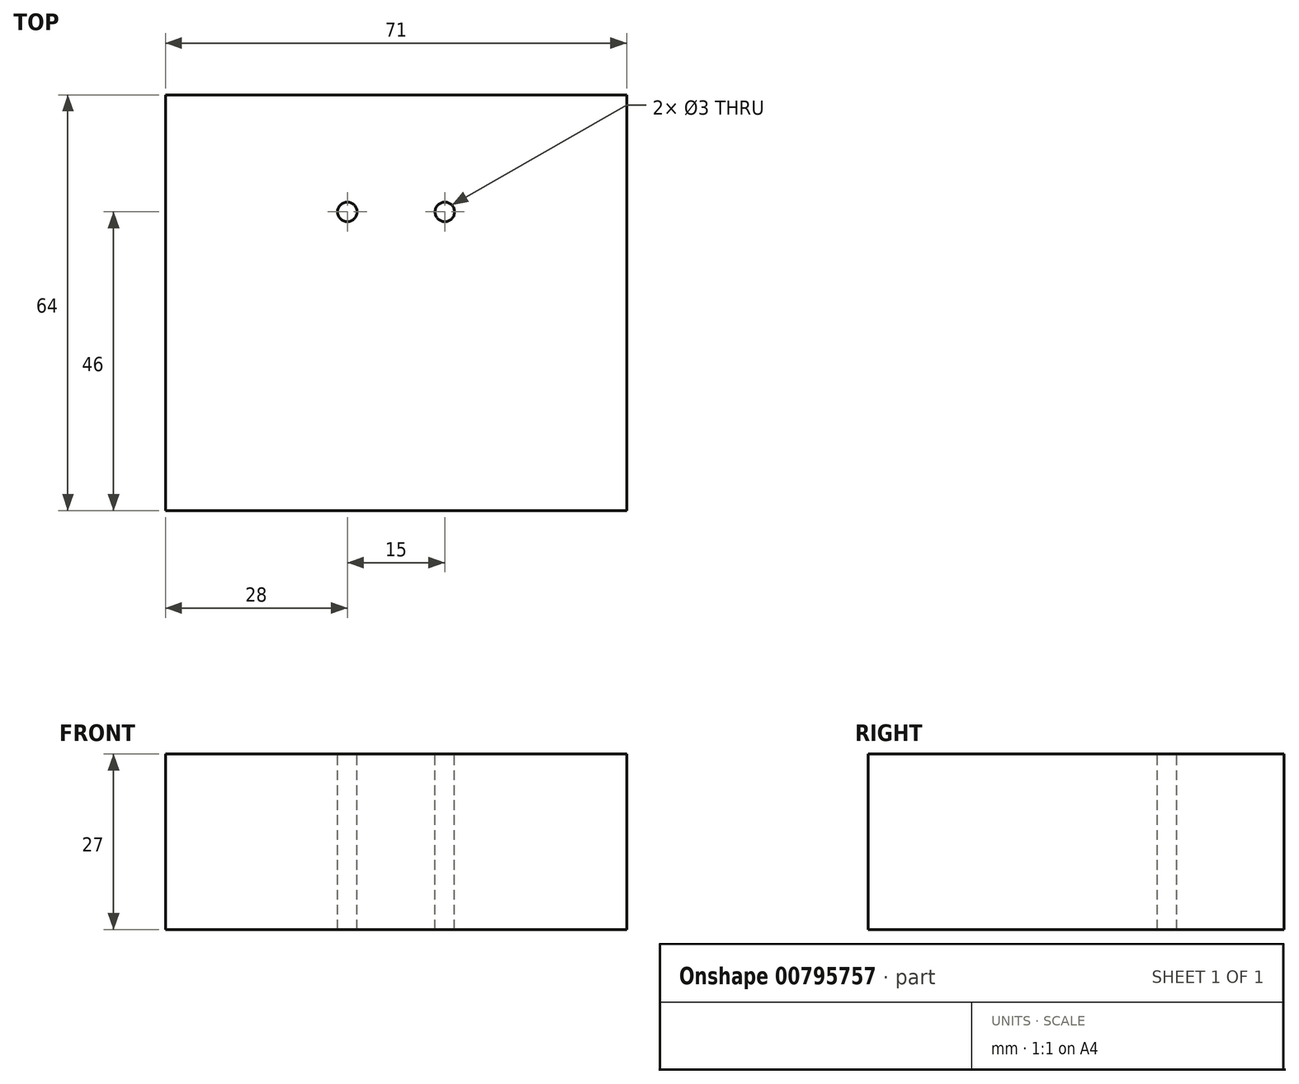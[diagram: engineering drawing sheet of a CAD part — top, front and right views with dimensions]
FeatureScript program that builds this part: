
annotation { "Feature Type Name" : "Feature", "Feature Type Description" : "" }
export const myFeature = defineFeature(function(context is Context, id is Id, definition is map)
    precondition{}
    {
        {
            var Q0;
            Q0=qCreatedBy(makeId("Top.planeOp"),FACE);
            var sketch = newSketch(context, id + "F0", { "sketchPlane" : qUnion([Q0])});
            skLineSegment(sketch, "E0.bottom", {"start": v(-35.5, 32) * mm, "end": v(35.5, 32) * mm});
            skLineSegment(sketch, "E0.top", {"start": v(-35.5, -32) * mm, "end": v(35.5, -32) * mm});
            skLineSegment(sketch, "E0.left", {"start": v(-35.5, 32) * mm, "end": v(-35.5, -32) * mm});
            skLineSegment(sketch, "E0.right", {"start": v(35.5, 32) * mm, "end": v(35.5, -32) * mm});
            skPoint(sketch, "E0.middle", {"position": v(0, 0) * mm});
            skSolve(sketch);
        }
        {
            var Q0;
            Q0=makeQuery(id+"F0.imprint","IMPRINT",FACE,{"disambiguationData":[TD([[makeQuery(id+"F0.imprint","IMPRINT",EDGE,{"derivedFrom":sQuery(id+"F0.wireOp",EDGE,"E0.bottom")}),-1.0]])]});
            extrude(context, id + "F1", {"entities" : qUnion([Q0]), "depth" : 27 * mm, "offsetDistance" : 25 * mm});
        }
        {
            var Q0;
            Q0=makeQuery(id+"F1.opExtrude","CAP_FACE",FACE,{"disambiguationData":[OSD([sQuery(id+"F0.wireOp",EDGE,"E0.bottom"),sQuery(id+"F0.wireOp",EDGE,"E0.top"),sQuery(id+"F0.wireOp",EDGE,"E0.left"),sQuery(id+"F0.wireOp",EDGE,"E0.right")])],"isStart":false});
            var sketch = newSketch(context, id + "F2", { "sketchPlane" : qUnion([Q0])});
            skCircle(sketch, "E1", {"center": v(-7.5, 14) * mm, "radius": 1.5 * mm});
            skLineSegment(sketch, "E2", {"start": v(0, 44.94) * mm, "end": v(0, -40.61) * mm});
            skPoint(sketch, "E2.endSnap0", {"position": v(0, -32) * mm});
            skCircle(sketch, "E3.MirrorC", {"center": v(7.5, 14) * mm, "radius": 1.5 * mm});
            skSolve(sketch);
        }
        {
            var Q0;
            Q0 = qSketchRegion(id + "F2", true);
            extrude(context, id + "F3", {"entities" : qUnion([Q0]), "operationType" : NewBodyOperationType.REMOVE, "endBound" : BoundingType.THROUGH_ALL, "oppositeDirection" : true, "depth" : 25 * mm, "offsetDistance" : 25 * mm});
        }
    });
